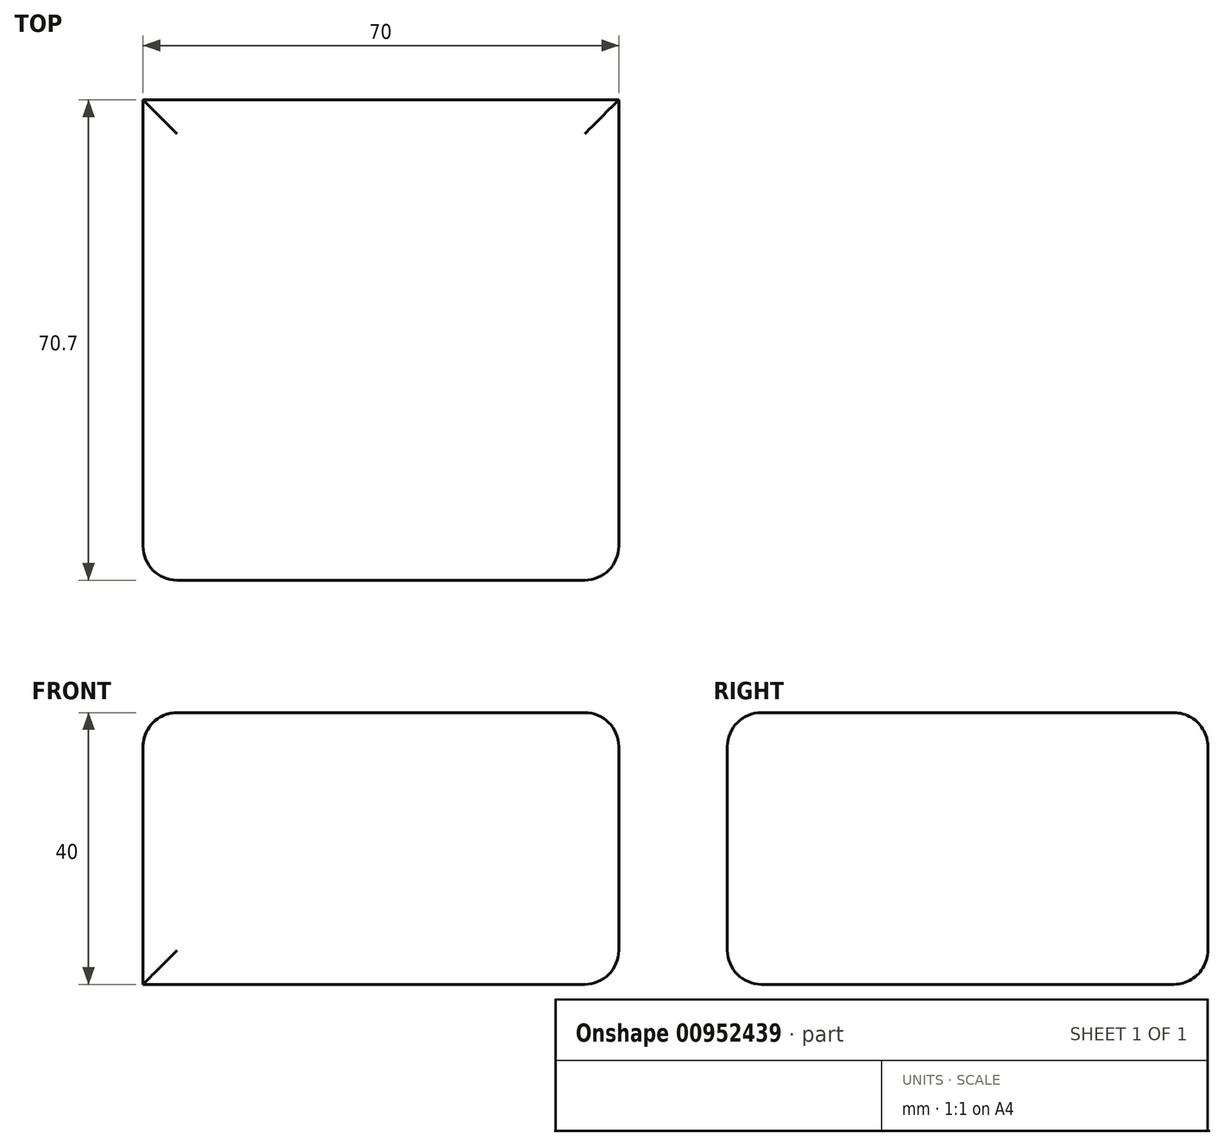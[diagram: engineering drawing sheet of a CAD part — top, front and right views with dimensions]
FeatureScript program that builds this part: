
annotation { "Feature Type Name" : "Feature", "Feature Type Description" : "" }
export const myFeature = defineFeature(function(context is Context, id is Id, definition is map)
    precondition{}
    {
        {
            var Q0;
            Q0=qCreatedBy(makeId("Front.planeOp"),FACE);
            var sketch = newSketch(context, id + "F0", { "sketchPlane" : qUnion([Q0])});
            skLineSegment(sketch, "E0", {"start": v(-70, 0) * mm, "end": v(-70, 40) * mm});
            skLineSegment(sketch, "E1", {"start": v(-70, 40) * mm, "end": v(0, 40) * mm});
            skLineSegment(sketch, "E2", {"start": v(0, 40) * mm, "end": v(0, 0) * mm});
            skLineSegment(sketch, "E3", {"start": v(0, 0) * mm, "end": v(-70, 0) * mm});
            skSolve(sketch);
        }
        {
            var Q0;
            Q0 = qSketchRegion(id + "F0", true);
            extrude(context, id + "F1", {"entities" : qUnion([Q0]), "endBound" : BoundingType.SYMMETRIC, "depth" : 70.7 * mm, "offsetDistance" : 25 * mm});
        }
        {
            var Q0;
            Q0=makeQuery(id+"F1.opExtrude","CAP_EDGE",EDGE,{"disambiguationData":[OSD([sQuery(id+"F0.wireOp",EDGE,"E1")])],"isStart":false});
            var Q1;
            Q1=makeQuery(id+"F1.opExtrude","SWEPT_EDGE",EDGE,{"disambiguationData":[OSD([sQuery(id+"F0.wireOp",EDGE,"E1"),sQuery(id+"F0.wireOp",EDGE,"E2")])]});
            var Q2;
            Q2=makeQuery(id+"F1.opExtrude","CAP_EDGE",EDGE,{"disambiguationData":[OSD([sQuery(id+"F0.wireOp",EDGE,"E2")])],"isStart":false});
            var Q3;
            Q3=makeQuery(id+"F1.opExtrude","CAP_EDGE",EDGE,{"disambiguationData":[OSD([sQuery(id+"F0.wireOp",EDGE,"E0")])],"isStart":false});
            var Q4;
            Q4=makeQuery(id+"F1.opExtrude","CAP_EDGE",EDGE,{"disambiguationData":[OSD([sQuery(id+"F0.wireOp",EDGE,"E3")])],"isStart":false});
            var Q5;
            Q5=makeQuery(id+"F1.opExtrude","SWEPT_EDGE",EDGE,{"disambiguationData":[OSD([sQuery(id+"F0.wireOp",EDGE,"E0"),sQuery(id+"F0.wireOp",EDGE,"E1")])]});
            var Q6;
            Q6=makeQuery(id+"F1.opExtrude","CAP_EDGE",EDGE,{"disambiguationData":[OSD([sQuery(id+"F0.wireOp",EDGE,"E1")])],"isStart":true});
            var Q7;
            Q7=makeQuery(id+"F1.opExtrude","SWEPT_EDGE",EDGE,{"disambiguationData":[OSD([sQuery(id+"F0.wireOp",EDGE,"E2"),sQuery(id+"F0.wireOp",EDGE,"E3")])]});
            var Q8;
            Q8=makeQuery(id+"F1.opExtrude","CAP_EDGE",EDGE,{"disambiguationData":[OSD([sQuery(id+"F0.wireOp",EDGE,"E3")])],"isStart":true});
            fillet(context, id + "F2", {"entities" : qUnion([Q0, Q1, Q2, Q3, Q4, Q5, Q6, Q7, Q8]), "radius" : 5 * mm, "tangentPropagation" : true, "allowEdgeOverflow" : false});
        }
    });
